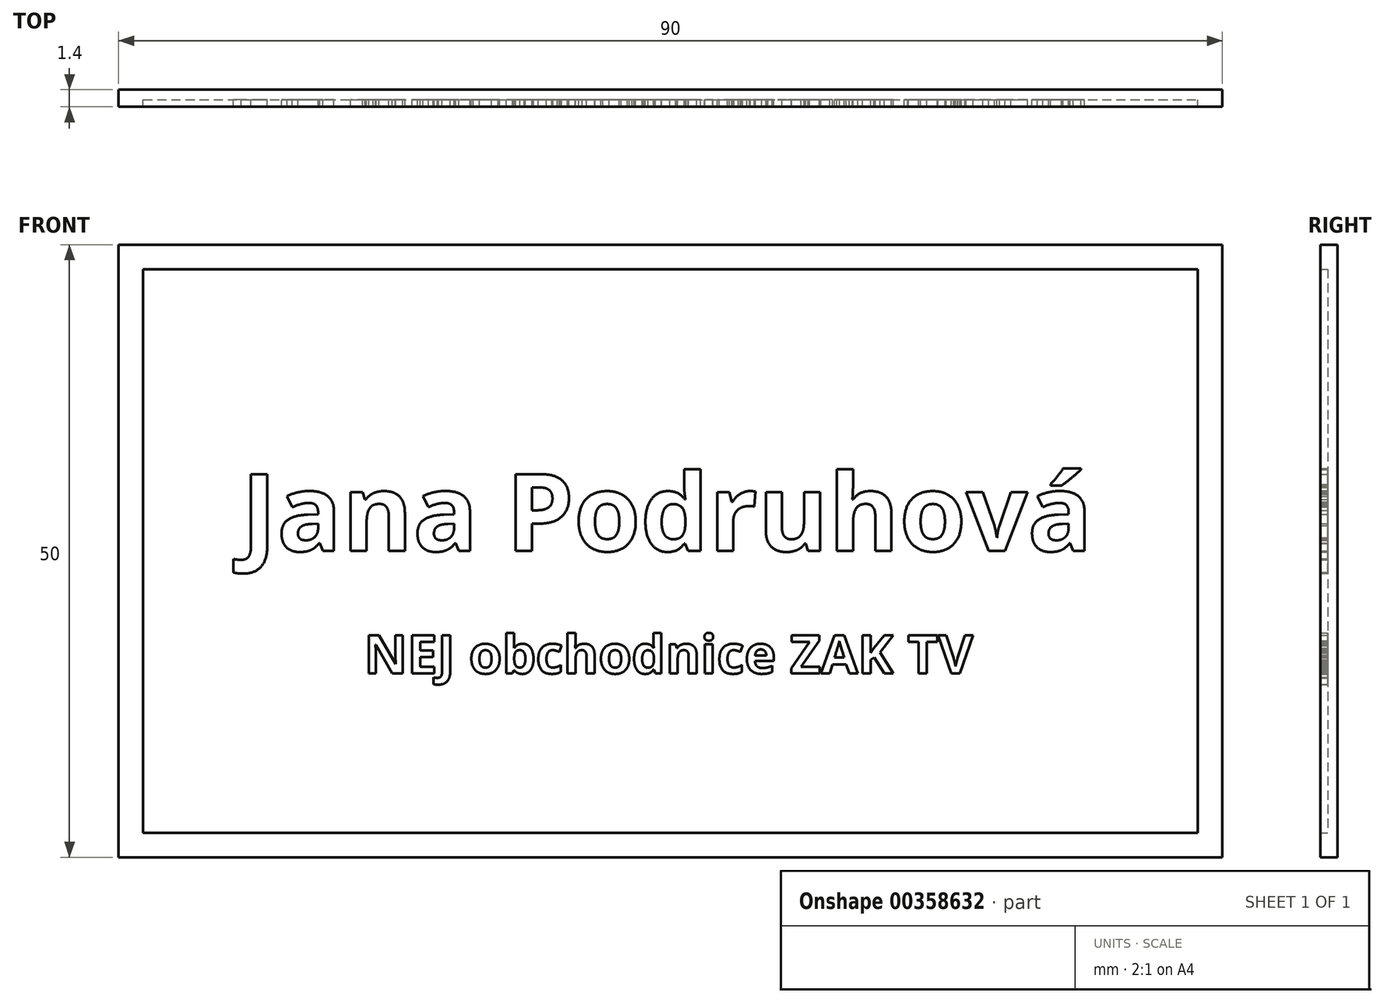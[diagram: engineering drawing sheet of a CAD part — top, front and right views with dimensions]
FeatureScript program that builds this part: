
annotation { "Feature Type Name" : "Feature", "Feature Type Description" : "" }
export const myFeature = defineFeature(function(context is Context, id is Id, definition is map)
    precondition{}
    {
        {
            var Q0;
            Q0=qCreatedBy(makeId("Front.planeOp"),FACE);
            var sketch = newSketch(context, id + "F0", { "sketchPlane" : qUnion([Q0])});
            skLineSegment(sketch, "E0.bottom", {"start": v(0, 0) * mm, "end": v(90, 0) * mm});
            skLineSegment(sketch, "E0.top", {"start": v(0, 50) * mm, "end": v(90, 50) * mm});
            skLineSegment(sketch, "E0.left", {"start": v(0, 0) * mm, "end": v(0, 50) * mm});
            skLineSegment(sketch, "E0.right", {"start": v(90, 0) * mm, "end": v(90, 50) * mm});
            skSolve(sketch);
        }
        {
            var Q0;
            Q0 = qSketchRegion(id + "F0", true);
            extrude(context, id + "F1", {"entities" : qUnion([Q0]), "depth" : 0.8 * mm});
        }
        {
            var Q0;
            Q0=makeQuery(id+"F1.opExtrude","CAP_FACE",FACE,{"disambiguationData":[OSD([sQuery(id+"F0.wireOp",EDGE,"E0.bottom"),sQuery(id+"F0.wireOp",EDGE,"E0.top"),sQuery(id+"F0.wireOp",EDGE,"E0.left"),sQuery(id+"F0.wireOp",EDGE,"E0.right")])],"isStart":false});
            var sketch = newSketch(context, id + "F2", { "sketchPlane" : qUnion([Q0])});
            skText(sketch, "E1", { "text": "Jana Podruhová", "fontName": "OpenSans-Bold.ttf"});
            skPoint(sketch, "E2", {"position": v(90, 25) * mm});
            const initialGuessF2  = {"E1": [0.01, 0.025, 1, 0, 0.00633]};
            skSetInitialGuess(sketch, initialGuessF2);
            skSolve(sketch);
        }
        {
            var Q0;
            Q0 = qSketchRegion(id + "F2", true);
            extrude(context, id + "F3", {"entities" : qUnion([Q0]), "operationType" : NewBodyOperationType.ADD, "depth" : 0.6 * mm});
        }
        {
            var Q0;
            {var subQ0=sQuery(id+"F0.wireOp",EDGE,"E0.left");var subQ1=sQuery(id+"F0.wireOp",EDGE,"E0.top");var subQ2=sQuery(id+"F0.wireOp",EDGE,"E0.right");var subQ3=sQuery(id+"F0.wireOp",EDGE,"E0.bottom");Q0=makeQuery(id+"F3.boolean.opBoolean","SPLIT",FACE,{"disambiguationData":[TD([makeQuery(id+"F1.opExtrude","SWEPT_FACE",FACE,{"disambiguationData":[OSD([subQ3])]})])],"derivedFrom":makeQuery(id+"F1.opExtrude","CAP_FACE",FACE,{"disambiguationData":[OSD([subQ3,subQ1,subQ0,subQ2])],"isStart":false})});}
            var sketch = newSketch(context, id + "F4", { "sketchPlane" : qUnion([Q0])});
            skText(sketch, "E3", { "text": "NEJ obchodnice ZAK TV", "fontName": "OpenSans-Bold.ttf"});
            const initialGuessF4  = {"E3": [0.02, 0.015, 1, 0, 0.00314]};
            skSetInitialGuess(sketch, initialGuessF4);
            skSolve(sketch);
        }
        {
            var Q0;
            Q0 = qSketchRegion(id + "F4", true);
            extrude(context, id + "F5", {"entities" : qUnion([Q0]), "operationType" : NewBodyOperationType.ADD, "depth" : 0.6 * mm});
        }
        {
            var Q0;
            {var subQ10=sQuery(id+"F0.wireOp",EDGE,"E0.top");var subQ65=sQuery(id+"F0.wireOp",EDGE,"E0.left");var subQ78=sQuery(id+"F0.wireOp",EDGE,"E0.right");var subQ89=sQuery(id+"F0.wireOp",EDGE,"E0.bottom");var subQ90=makeQuery(id+"F1.opExtrude","SWEPT_FACE",FACE,{"disambiguationData":[OSD([subQ89])]});Q0=makeQuery(id+"F5.boolean.opBoolean","SPLIT",FACE,{"disambiguationData":[TD([subQ90])],"derivedFrom":makeQuery(id+"F3.boolean.opBoolean","SPLIT",FACE,{"disambiguationData":[TD([subQ90])],"derivedFrom":makeQuery(id+"F1.opExtrude","CAP_FACE",FACE,{"disambiguationData":[OSD([subQ89,subQ10,subQ65,subQ78])],"isStart":false})})});}
            var sketch = newSketch(context, id + "F6", { "sketchPlane" : qUnion([Q0])});
            skLineSegment(sketch, "E4.bottom", {"start": v(0, 50) * mm, "end": v(90, 50) * mm});
            skLineSegment(sketch, "E4.top", {"start": v(0, 0) * mm, "end": v(90, 0) * mm});
            skLineSegment(sketch, "E4.left", {"start": v(0, 50) * mm, "end": v(0, 0) * mm});
            skLineSegment(sketch, "E4.right", {"start": v(90, 50) * mm, "end": v(90, 0) * mm});
            skLineSegment(sketch, "E5.bottom", {"start": v(2, 48) * mm, "end": v(88, 48) * mm});
            skLineSegment(sketch, "E5.top", {"start": v(2, 2) * mm, "end": v(88, 2) * mm});
            skLineSegment(sketch, "E5.left", {"start": v(2, 48) * mm, "end": v(2, 2) * mm});
            skLineSegment(sketch, "E5.right", {"start": v(88, 48) * mm, "end": v(88, 2) * mm});
            skSolve(sketch);
        }
        {
            var Q0;
            Q0 = qSketchRegion(id + "F6", true);
            extrude(context, id + "F7", {"entities" : qUnion([Q0]), "operationType" : NewBodyOperationType.ADD, "depth" : 0.6 * mm});
        }
    });
